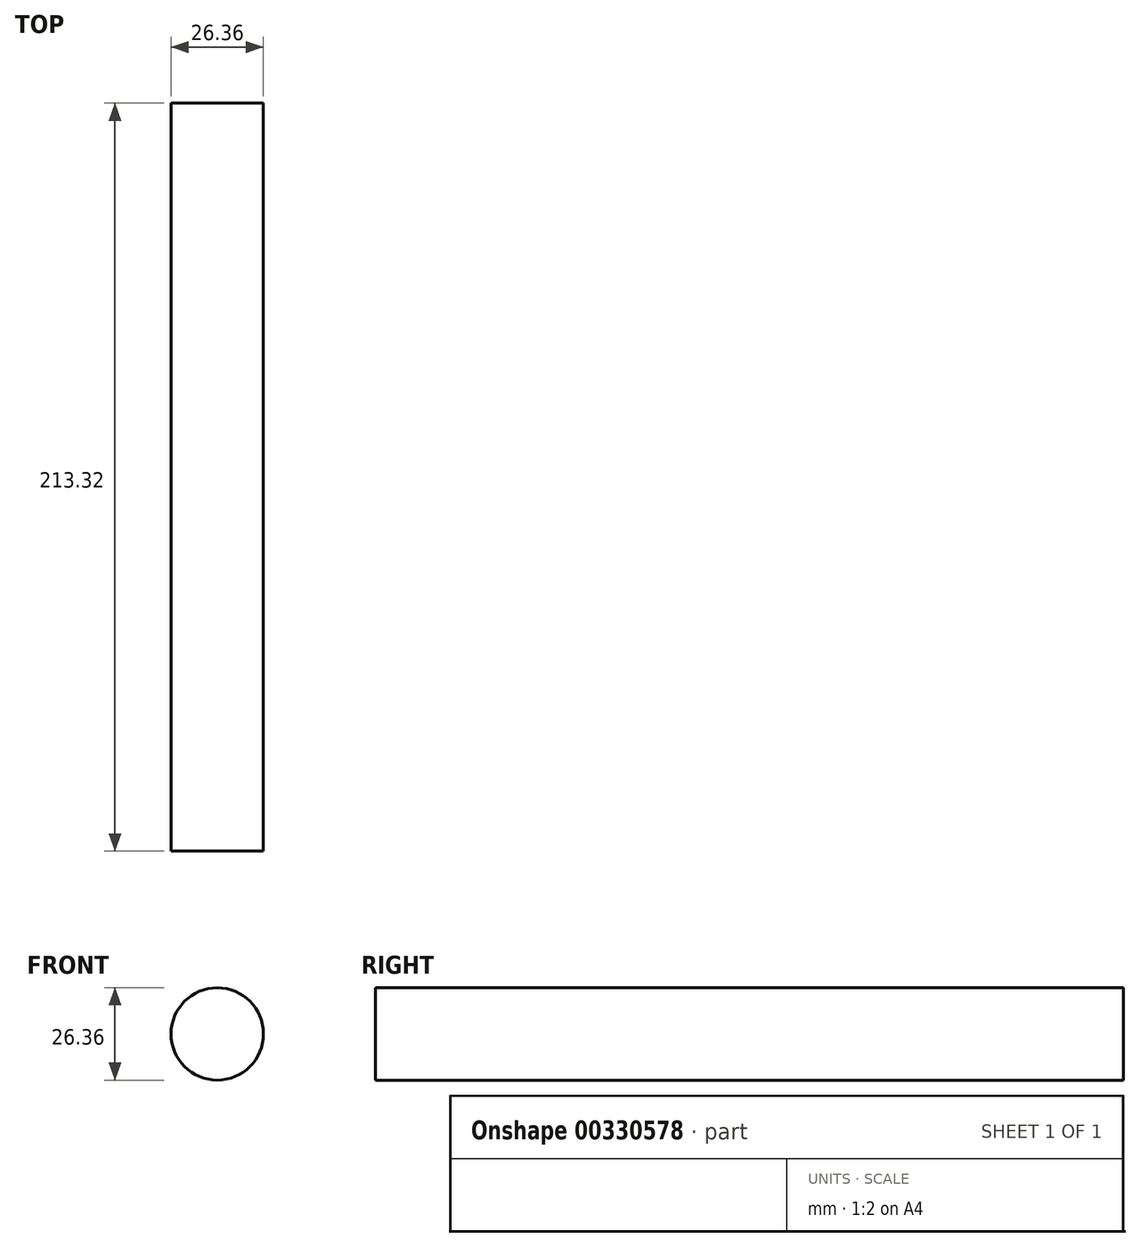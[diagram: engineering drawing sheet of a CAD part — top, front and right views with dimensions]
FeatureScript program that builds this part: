
annotation { "Feature Type Name" : "Feature", "Feature Type Description" : "" }
export const myFeature = defineFeature(function(context is Context, id is Id, definition is map)
    precondition{}
    {
        {
            var Q0;
            Q0=qCreatedBy(makeId("Front.planeOp"),FACE);
            var sketch = newSketch(context, id + "F0", { "sketchPlane" : qUnion([Q0])});
            skCircle(sketch, "E0", {"center": v(0.35, -7.56) * mm, "radius": 13.18 * mm});
            skSolve(sketch);
        }
        {
            var Q0;
            Q0=makeQuery(id+"F0.imprint","IMPRINT",FACE,{"disambiguationData":[TD([[makeQuery(id+"F0.imprint","IMPRINT",EDGE,{"derivedFrom":sQuery(id+"F0.wireOp",EDGE,"E0")}),1.0]])]});
            var Q1;
            Q1 = qSketchRegion(id + "F0", true);
            extrude(context, id + "F1", {"entities" : qUnion([Q0, Q1]), "depth" : 213.32 * mm});
        }
    });
